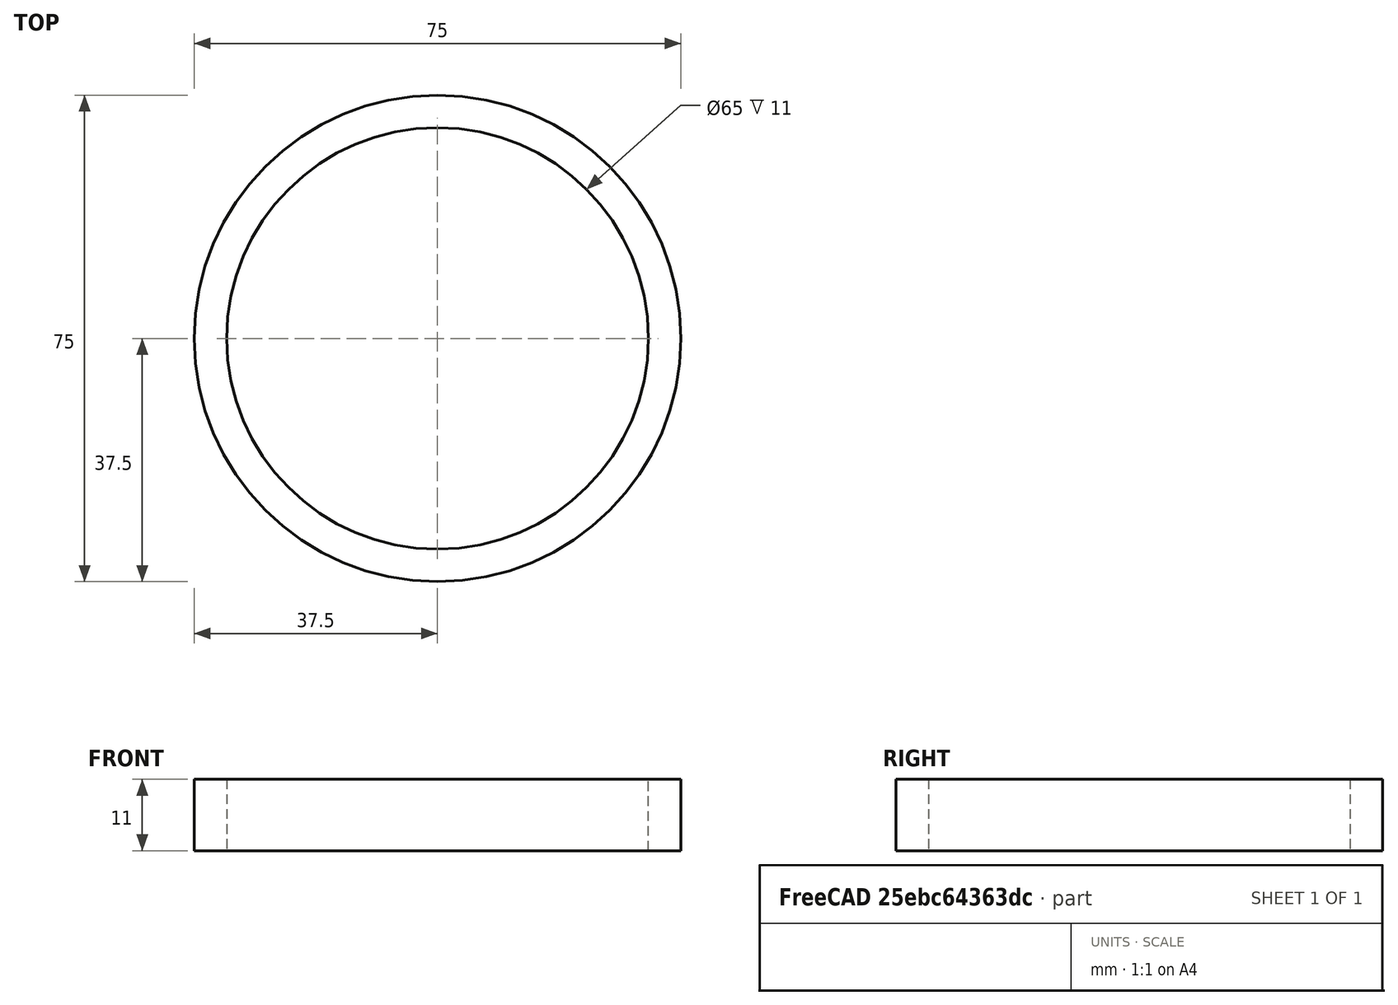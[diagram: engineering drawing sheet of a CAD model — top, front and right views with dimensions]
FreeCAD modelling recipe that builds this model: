
FCSTD DOCUMENT  (FreeCAD 0.19R24276 (Git))
Label: Ring_45x75x11_OUT
License: All rights reserved
LicenseURL: http://en.wikipedia.org/wiki/All_rights_reserved
objects: Sketcher::SketchObject×1, PartDesign::Pad×1, PartDesign::Body×1
note: 4 computed .brp shape members not serialized (recipe doc carries the construction recipe); baked Part::Feature solids carry a one-line shape summary decoded from their .brp

FEATURE [Sketcher::SketchObject] Sketch
  FullyConstrained = true
  MapMode = 5
  Support = -> [XY_Plane]
  sketch-geometry (2):
    g0: Circle CenterX=0 CenterY=0 CenterZ=0 NormalX=0 NormalY=0 NormalZ=1 AngleXU=0 Radius=32.5
    g1: Circle CenterX=0 CenterY=0 CenterZ=0 NormalX=0 NormalY=0 NormalZ=1 AngleXU=0 Radius=37.5
  constraints (4):
    c: Coincident(g1,g0)
    c: Diameter(g1) = 75
    c: Diameter(g0) = 65
    c: Coincident(g0,g-1)
FEATURE [PartDesign::Pad] Pad
  Direction = (1,1,1)
  Length = 11
  Length2 = 100
  Profile = -> Sketch
  Type = 0
FEATURE [PartDesign::Body] Body  label="Body_ring_out"
  Group = -> [Sketch,Pad]
  Origin = -> Origin
  Tip = -> Pad
